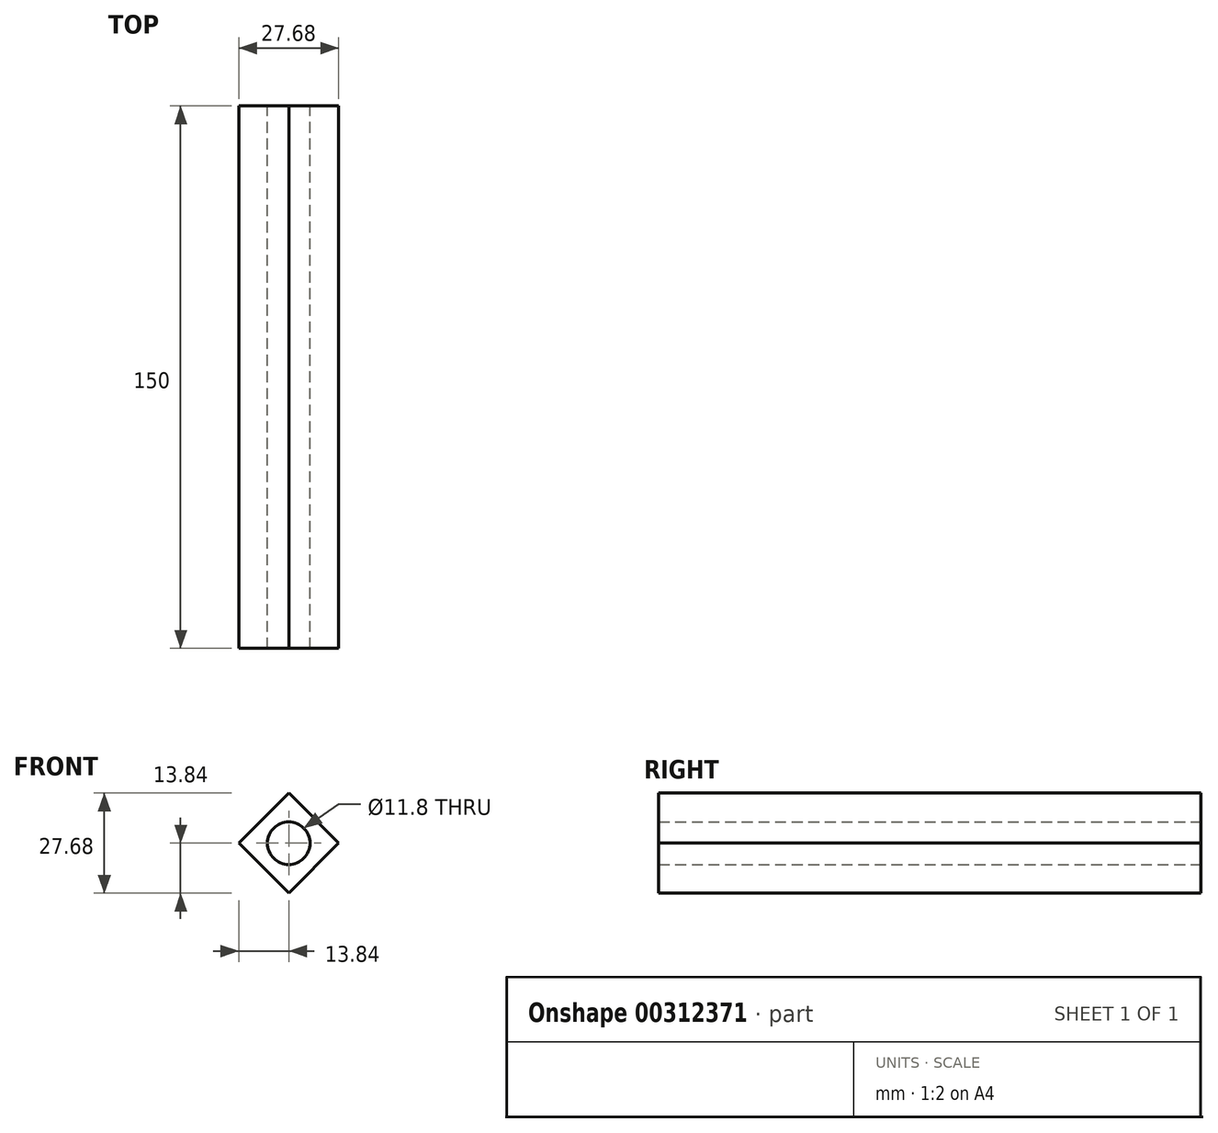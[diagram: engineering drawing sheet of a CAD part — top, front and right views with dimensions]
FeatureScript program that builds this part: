
annotation { "Feature Type Name" : "Feature", "Feature Type Description" : "" }
export const myFeature = defineFeature(function(context is Context, id is Id, definition is map)
    precondition{}
    {
        {
            var Q0;
            Q0=qCreatedBy(makeId("Front.planeOp"),FACE);
            var sketch = newSketch(context, id + "F0", { "sketchPlane" : qUnion([Q0])});
            skLineSegment(sketch, "E0", {"start": v(-27.68, 0) * mm, "end": v(-13.84, 13.84) * mm});
            skLineSegment(sketch, "E1", {"start": v(-13.84, 13.84) * mm, "end": v(0, 0) * mm});
            skLineSegment(sketch, "E2", {"start": v(-27.68, 0) * mm, "end": v(-13.84, -13.84) * mm});
            skLineSegment(sketch, "E3", {"start": v(-13.84, -13.84) * mm, "end": v(0, 0) * mm});
            skPoint(sketch, "E4", {"position": v(-13.84, 0) * mm});
            skCircle(sketch, "E5", {"center": v(-13.84, 0) * mm, "radius": 5.9 * mm});
            skLineSegment(sketch, "E6", {"start": v(0, 0) * mm, "end": v(19.58, 0) * mm});
            skLineSegment(sketch, "E7", {"start": v(9.8, 0) * mm, "end": v(9.8, 9.79) * mm});
            skLineSegment(sketch, "E8", {"start": v(9.8, 0) * mm, "end": v(9.8, -9.79) * mm});
            skLineSegment(sketch, "E9", {"start": v(9.8, 9.79) * mm, "end": v(19.58, 0) * mm});
            skLineSegment(sketch, "E10", {"start": v(19.58, 0) * mm, "end": v(9.8, -9.79) * mm});
            skLineSegment(sketch, "E11", {"start": v(9.8, -9.79) * mm, "end": v(0, 0) * mm});
            skLineSegment(sketch, "E12", {"start": v(0, 0) * mm, "end": v(9.8, 9.79) * mm});
            skSolve(sketch);
        }
        {
            var Q0;
            {var subQ0=sQuery(id+"F0.wireOp",EDGE,"E2");Q0=makeQuery(id+"F0.imprint","IMPRINT",FACE,{"disambiguationData":[TD([[makeQuery(id+"F0.imprint","IMPRINT",EDGE,{"derivedFrom":subQ0}),1.0]])]});}
            var Q1;
            {var subQ1=sQuery(id+"F0.wireOp",EDGE,"E0");Q1=makeQuery(id+"F0.imprint","IMPRINT",FACE,{"disambiguationData":[TD([[makeQuery(id+"F0.imprint","IMPRINT",EDGE,{"derivedFrom":subQ1}),-1.0]])]});}
            extrude(context, id + "F1", {"entities" : qUnion([Q0, Q1]), "depth" : 150 * mm});
        }
    });
